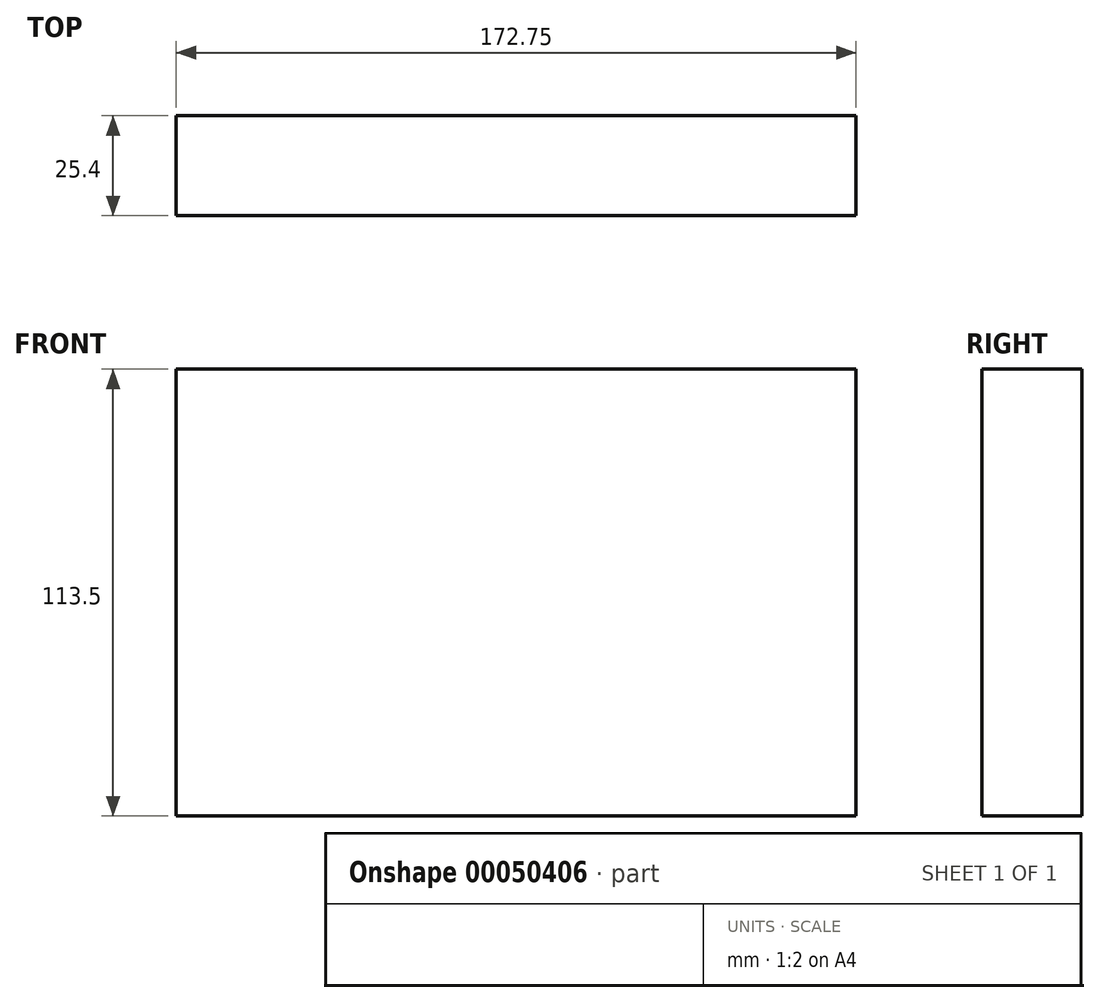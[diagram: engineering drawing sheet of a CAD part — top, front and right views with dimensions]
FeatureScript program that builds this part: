
annotation { "Feature Type Name" : "Feature", "Feature Type Description" : "" }
export const myFeature = defineFeature(function(context is Context, id is Id, definition is map)
    precondition{}
    {
        {
            var Q0;
            Q0=qCreatedBy(makeId("Front.planeOp"),FACE);
            var sketch = newSketch(context, id + "F0", { "sketchPlane" : qUnion([Q0])});
            skLineSegment(sketch, "E0.bottom", {"start": v(-78.92, 54.18) * mm, "end": v(93.83, 54.18) * mm});
            skLineSegment(sketch, "E0.top", {"start": v(-78.92, -59.32) * mm, "end": v(93.83, -59.32) * mm});
            skLineSegment(sketch, "E0.left", {"start": v(-78.92, 54.18) * mm, "end": v(-78.92, -59.32) * mm});
            skLineSegment(sketch, "E0.right", {"start": v(93.83, 54.18) * mm, "end": v(93.83, -59.32) * mm});
            skSolve(sketch);
        }
        {
            var Q0;
            Q0=makeQuery(id+"F0.imprint","IMPRINT",FACE,{"disambiguationData":[TD([[makeQuery(id+"F0.imprint","IMPRINT",EDGE,{"derivedFrom":sQuery(id+"F0.wireOp",EDGE,"E0.bottom")}),-1.0]])]});
            extrude(context, id + "F1", {"entities" : qUnion([Q0]), "depth" : 25.4 * mm});
        }
    });
